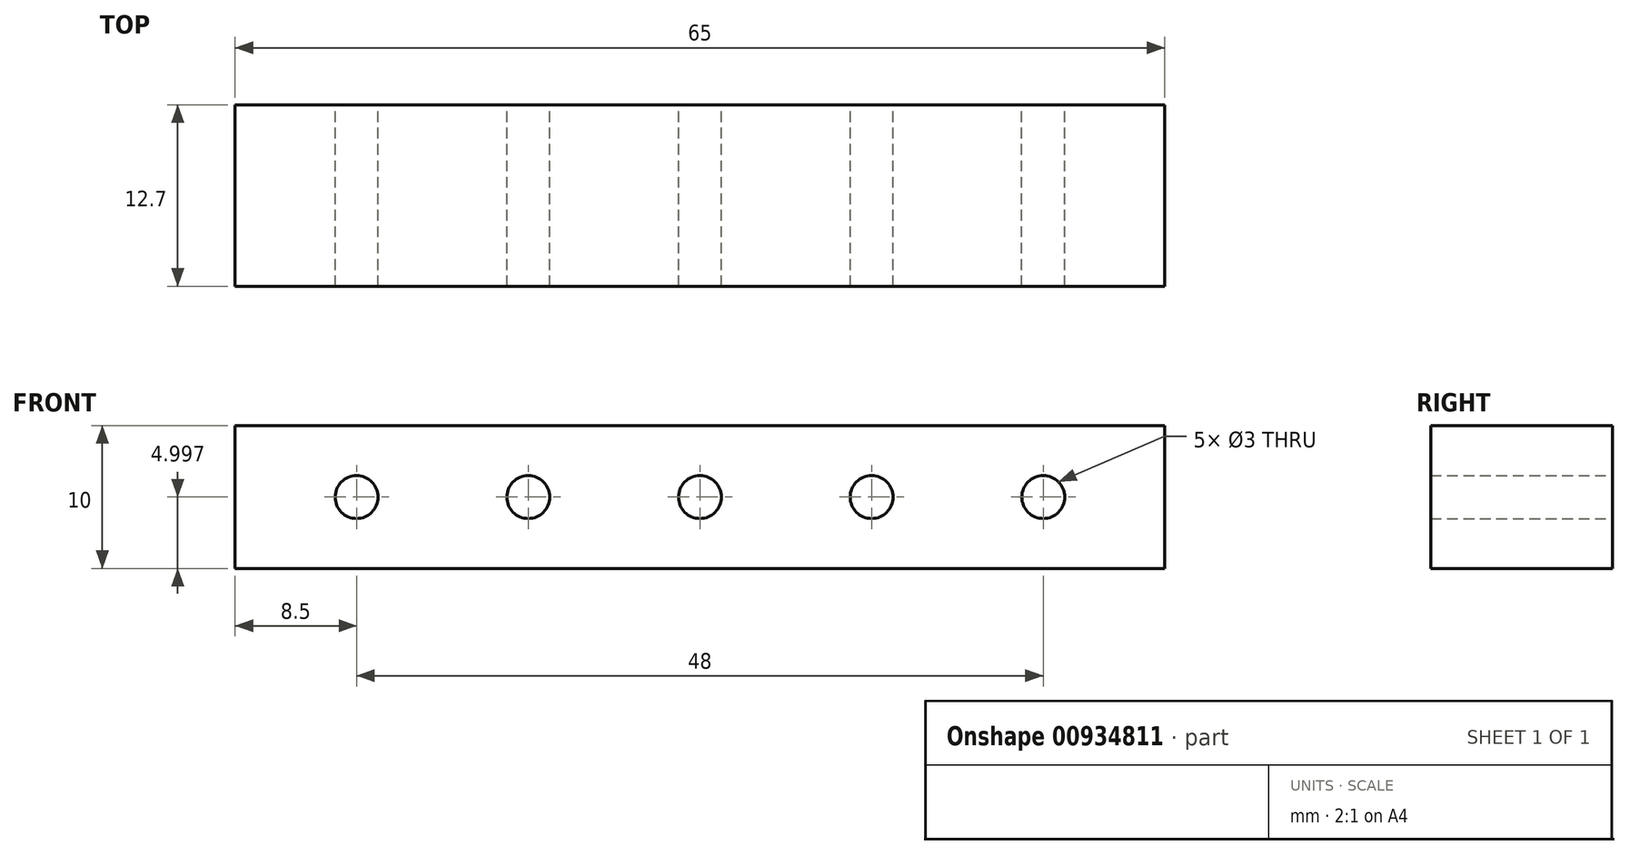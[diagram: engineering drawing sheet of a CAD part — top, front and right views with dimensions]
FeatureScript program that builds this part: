
annotation { "Feature Type Name" : "Feature", "Feature Type Description" : "" }
export const myFeature = defineFeature(function(context is Context, id is Id, definition is map)
    precondition{}
    {
        {
            var Q0;
            Q0=qCreatedBy(makeId("Front.planeOp"),FACE);
            var sketch = newSketch(context, id + "F0", { "sketchPlane" : qUnion([Q0])});
            skLineSegment(sketch, "E0.bottom", {"start": v(-65, 28.43) * mm, "end": v(0, 28.43) * mm});
            skLineSegment(sketch, "E0.top", {"start": v(-65, 18.43) * mm, "end": v(0, 18.43) * mm});
            skLineSegment(sketch, "E0.left", {"start": v(-65, 28.43) * mm, "end": v(-65, 18.43) * mm});
            skLineSegment(sketch, "E0.right", {"start": v(0, 28.43) * mm, "end": v(0, 18.43) * mm});
            skLineSegment(sketch, "E1", {"start": v(-65, 23.43) * mm, "end": v(0, 23.43) * mm, "construction": true});
            skCircle(sketch, "E2", {"center": v(-56.5, 23.43) * mm, "radius": 1.5 * mm});
            skCircle(sketch, "E3.1.0.0", {"center": v(-44.5, 23.43) * mm, "radius": 1.5 * mm});
            skCircle(sketch, "E3.2.0.0", {"center": v(-32.5, 23.43) * mm, "radius": 1.5 * mm});
            skCircle(sketch, "E3.3.0.0", {"center": v(-20.5, 23.43) * mm, "radius": 1.5 * mm});
            skLineSegment(sketch, "E3.direction1", {"start": v(-56.5, 23.43) * mm, "end": v(-44.5, 23.43) * mm, "construction": true});
            skCircle(sketch, "E4.0.4.0", {"center": v(-8.5, 23.43) * mm, "radius": 1.5 * mm});
            skSolve(sketch);
        }
        {
            var Q0;
            Q0 = qSketchRegion(id + "F0", true);
            extrude(context, id + "F1", {"entities" : qUnion([Q0]), "depth" : 12.7 * mm, "offsetDistance" : 25 * mm});
        }
    });
